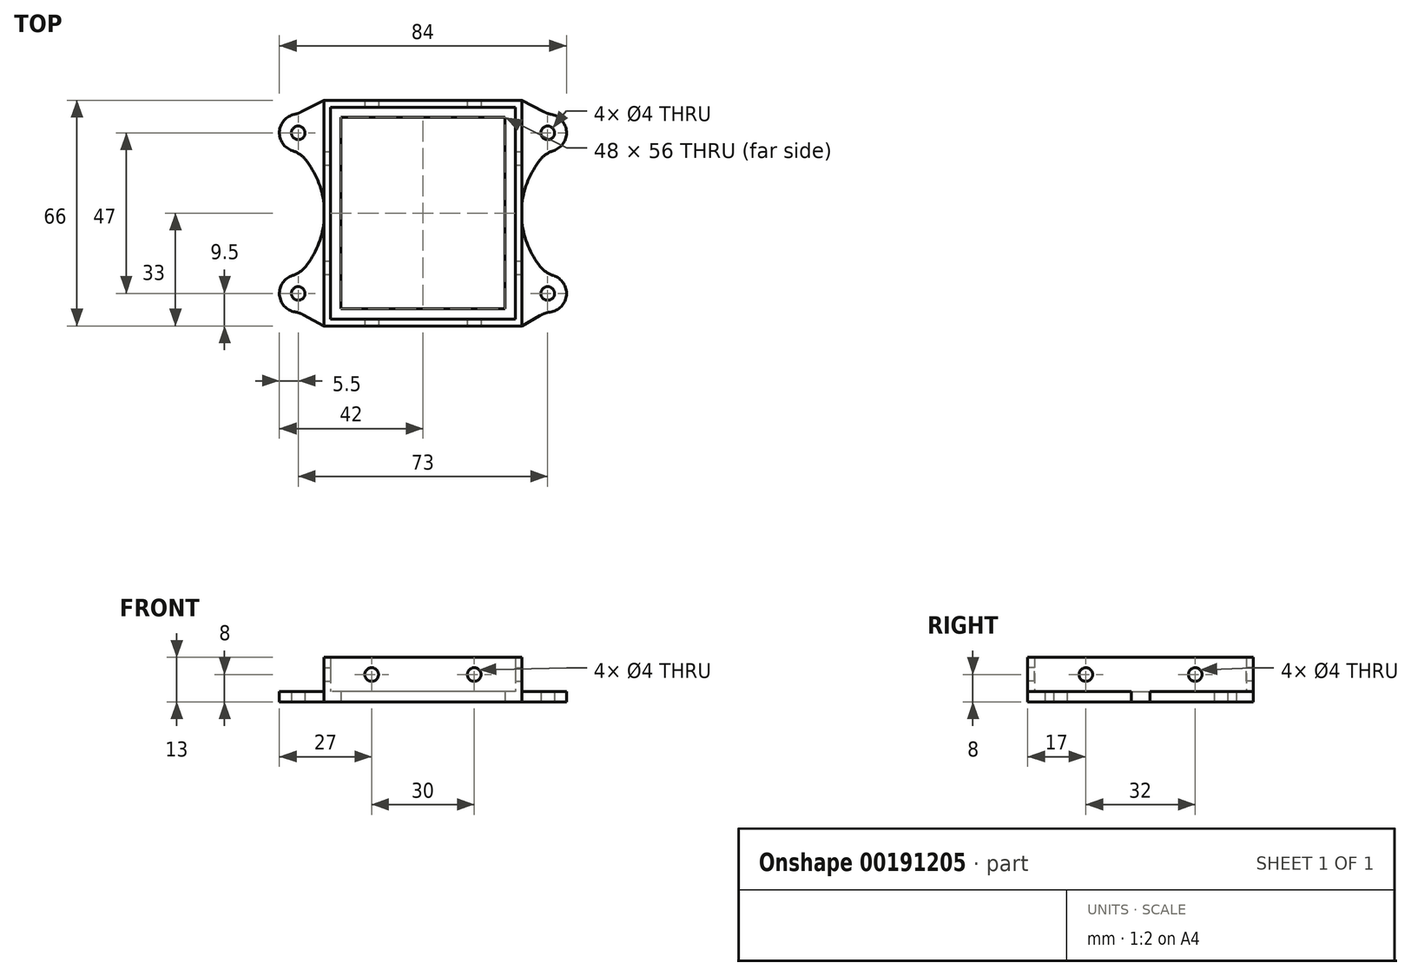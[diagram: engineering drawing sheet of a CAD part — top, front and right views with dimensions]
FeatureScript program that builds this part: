
annotation { "Feature Type Name" : "Feature", "Feature Type Description" : "" }
export const myFeature = defineFeature(function(context is Context, id is Id, definition is map)
    precondition{}
    {
        {
            var Q0;
            Q0=qCreatedBy(makeId("Top.planeOp"),FACE);
            var sketch = newSketch(context, id + "F0", { "sketchPlane" : qUnion([Q0])});
            skLineSegment(sketch, "E0.bottom", {"start": v(29, -33) * mm, "end": v(-29, -33) * mm});
            skLineSegment(sketch, "E0.top", {"start": v(29, 33) * mm, "end": v(-29, 33) * mm});
            skLineSegment(sketch, "E0.left", {"start": v(29, -2.74) * mm, "end": v(29, 2.74) * mm});
            skLineSegment(sketch, "E0.right", {"start": v(-29, -2.74) * mm, "end": v(-29, 2.74) * mm});
            skPoint(sketch, "E0.middle", {"position": v(0, 0) * mm});
            skCircle(sketch, "E1", {"center": v(-36.5, 23.5) * mm, "radius": 2 * mm});
            skCircle(sketch, "E2", {"center": v(-36.5, -23.5) * mm, "radius": 2 * mm});
            skCircle(sketch, "E3", {"center": v(36.5, -23.5) * mm, "radius": 2 * mm});
            skCircle(sketch, "E4", {"center": v(36.5, 23.5) * mm, "radius": 2 * mm});
            skArc(sketch, "E5", {"start": v(38.16, 18.26) * mm, "mid": v(41.99, 23.84) * mm, "end": v(37.51, 28.9) * mm});
            skArc(sketch, "E6", {"start": v(37.2, -28.96) * mm, "mid": v(41.98, -24) * mm, "end": v(38.16, -18.26) * mm});
            skArc(sketch, "E7", {"start": v(-38.16, -18.26) * mm, "mid": v(-41.99, -23.87) * mm, "end": v(-37.44, -28.92) * mm});
            skArc(sketch, "E8", {"start": v(-37.6, 28.89) * mm, "mid": v(-42, 23.8) * mm, "end": v(-38.16, 18.26) * mm});
            skArc(sketch, "E9", {"start": v(-34.34, -15.64) * mm, "mid": v(-28.85, 0) * mm, "end": v(-34.34, 15.64) * mm});
            skArc(sketch, "E10", {"start": v(34.34, 15.64) * mm, "mid": v(28.85, 0) * mm, "end": v(34.34, -15.64) * mm});
            skLineSegment(sketch, "E11", {"start": v(-29, 33) * mm, "end": v(-35.52, 29.62) * mm});
            skLineSegment(sketch, "E12", {"start": v(29, 33) * mm, "end": v(35.24, 29.7) * mm});
            skLineSegment(sketch, "E13", {"start": v(-35, -29.76) * mm, "end": v(-29, -33) * mm});
            skLineSegment(sketch, "E14", {"start": v(34.19, -29.98) * mm, "end": v(29, -33) * mm});
            skPoint(sketch, "E15.visualSharp", {"position": v(35.92, -28.97) * mm});
            skArc(sketch, "E15.filletArc", {"start": v(37.2, -28.96) * mm, "mid": v(35.64, -29.32) * mm, "end": v(34.19, -29.98) * mm});
            skPoint(sketch, "E16.visualSharp", {"position": v(-36.41, -29) * mm});
            skArc(sketch, "E16.filletArc", {"start": v(-35, -29.76) * mm, "mid": v(-36.18, -29.24) * mm, "end": v(-37.44, -28.92) * mm});
            skPoint(sketch, "E17.visualSharp", {"position": v(-36.74, 29) * mm});
            skArc(sketch, "E17.filletArc", {"start": v(-37.6, 28.89) * mm, "mid": v(-36.54, 29.18) * mm, "end": v(-35.52, 29.62) * mm});
            skPoint(sketch, "E18.visualSharp", {"position": v(36.56, 29) * mm});
            skArc(sketch, "E18.filletArc", {"start": v(35.24, 29.7) * mm, "mid": v(36.35, 29.22) * mm, "end": v(37.51, 28.9) * mm});
            skPoint(sketch, "E19.visualSharp", {"position": v(36.5, 18) * mm});
            skArc(sketch, "E19.filletArc", {"start": v(38.16, 18.26) * mm, "mid": v(36.06, 17.23) * mm, "end": v(34.34, 15.64) * mm});
            skPoint(sketch, "E20.visualSharp", {"position": v(36.5, -18) * mm});
            skArc(sketch, "E20.filletArc", {"start": v(34.34, -15.64) * mm, "mid": v(36.06, -17.23) * mm, "end": v(38.16, -18.26) * mm});
            skPoint(sketch, "E21.visualSharp", {"position": v(-36.5, -18) * mm});
            skArc(sketch, "E21.filletArc", {"start": v(-38.16, -18.26) * mm, "mid": v(-36.06, -17.23) * mm, "end": v(-34.34, -15.64) * mm});
            skPoint(sketch, "E22.visualSharp", {"position": v(-36.5, 18) * mm});
            skArc(sketch, "E22.filletArc", {"start": v(-34.34, 15.64) * mm, "mid": v(-36.06, 17.23) * mm, "end": v(-38.16, 18.26) * mm});
            skLineSegment(sketch, "E23.bottom", {"start": v(24, -28) * mm, "end": v(-24, -28) * mm});
            skLineSegment(sketch, "E23.top", {"start": v(24, 28) * mm, "end": v(-24, 28) * mm});
            skLineSegment(sketch, "E23.left", {"start": v(24, -28) * mm, "end": v(24, 28) * mm});
            skLineSegment(sketch, "E23.right", {"start": v(-24, -28) * mm, "end": v(-24, 28) * mm});
            skSolve(sketch);
        }
        {
            var Q0;
            Q0 = qSketchRegion(id + "F0", true);
            extrude(context, id + "F1", {"entities" : qUnion([Q0]), "depth" : 3 * mm});
        }
        {
            var Q0;
            Q0=makeQuery(id+"F1.opExtrude","CAP_FACE",FACE,{"disambiguationData":[OSD([sQuery(id+"F0.wireOp",EDGE,"E0.bottom"),sQuery(id+"F0.wireOp",EDGE,"E0.top"),sQuery(id+"F0.wireOp",EDGE,"E0.left"),sQuery(id+"F0.wireOp",EDGE,"E0.right"),sQuery(id+"F0.wireOp",EDGE,"E1"),sQuery(id+"F0.wireOp",EDGE,"E2"),sQuery(id+"F0.wireOp",EDGE,"E3"),sQuery(id+"F0.wireOp",EDGE,"E4"),sQuery(id+"F0.wireOp",EDGE,"E5"),sQuery(id+"F0.wireOp",EDGE,"E6"),sQuery(id+"F0.wireOp",EDGE,"E7"),sQuery(id+"F0.wireOp",EDGE,"E8"),sQuery(id+"F0.wireOp",EDGE,"E9"),sQuery(id+"F0.wireOp",EDGE,"E10"),sQuery(id+"F0.wireOp",EDGE,"E11"),sQuery(id+"F0.wireOp",EDGE,"E12"),sQuery(id+"F0.wireOp",EDGE,"E13"),sQuery(id+"F0.wireOp",EDGE,"E14"),sQuery(id+"F0.wireOp",EDGE,"E15.filletArc"),sQuery(id+"F0.wireOp",EDGE,"E16.filletArc"),sQuery(id+"F0.wireOp",EDGE,"E17.filletArc"),sQuery(id+"F0.wireOp",EDGE,"E18.filletArc"),sQuery(id+"F0.wireOp",EDGE,"E19.filletArc"),sQuery(id+"F0.wireOp",EDGE,"E20.filletArc"),sQuery(id+"F0.wireOp",EDGE,"E21.filletArc"),sQuery(id+"F0.wireOp",EDGE,"E22.filletArc")])],"isStart":false});
            var sketch = newSketch(context, id + "F2", { "sketchPlane" : qUnion([Q0])});
            skLineSegment(sketch, "E24.bottom", {"start": v(29, -33) * mm, "end": v(-29, -33) * mm});
            skLineSegment(sketch, "E24.top", {"start": v(29, 33) * mm, "end": v(-29, 33) * mm});
            skLineSegment(sketch, "E24.left", {"start": v(29, -33) * mm, "end": v(29, 33) * mm});
            skLineSegment(sketch, "E24.right", {"start": v(-29, -33) * mm, "end": v(-29, 33) * mm});
            skPoint(sketch, "E24.middle", {"position": v(0, 0) * mm});
            skLineSegment(sketch, "E25.bottom", {"start": v(27, -31) * mm, "end": v(-27, -31) * mm});
            skLineSegment(sketch, "E25.top", {"start": v(27, 31) * mm, "end": v(-27, 31) * mm});
            skLineSegment(sketch, "E25.left", {"start": v(27, -31) * mm, "end": v(27, 31) * mm});
            skLineSegment(sketch, "E25.right", {"start": v(-27, -31) * mm, "end": v(-27, 31) * mm});
            skSolve(sketch);
        }
        {
            var Q0;
            Q0 = qSketchRegion(id + "F2", true);
            extrude(context, id + "F3", {"entities" : qUnion([Q0]), "operationType" : NewBodyOperationType.ADD, "depth" : 10 * mm});
        }
        {
            var Q0;
            Q0=makeQuery(id+"F3.boolean.opBoolean","MERGE",FACE,{"derivedFrom":[makeQuery(id+"F1.opExtrude","SWEPT_FACE",FACE,{"disambiguationData":[OSD([sQuery(id+"F0.wireOp",EDGE,"E0.bottom")])]}),makeQuery(id+"F3.opExtrude","SWEPT_FACE",FACE,{"disambiguationData":[OSD([sQuery(id+"F2.wireOp",EDGE,"E24.bottom")])]})]});
            var sketch = newSketch(context, id + "F4", { "sketchPlane" : qUnion([Q0])});
            skCircle(sketch, "E26", {"center": v(-15, 8) * mm, "radius": 2 * mm});
            skPoint(sketch, "E26.centerSnap0", {"position": v(-29, 8) * mm});
            skCircle(sketch, "E27", {"center": v(15, 8) * mm, "radius": 2 * mm});
            skPoint(sketch, "E27.centerSnap0", {"position": v(29, 8) * mm});
            skSolve(sketch);
        }
        {
            var Q0;
            Q0 = qSketchRegion(id + "F4", true);
            extrude(context, id + "F5", {"entities" : qUnion([Q0]), "operationType" : NewBodyOperationType.REMOVE, "oppositeDirection" : true, "depth" : 150 * mm});
        }
        {
            var Q0;
            Q0=makeQuery(id+"F3.boolean.opBoolean","MERGE",FACE,{"derivedFrom":[makeQuery(id+"F1.opExtrude","SWEPT_FACE",FACE,{"disambiguationData":[OSD([sQuery(id+"F0.wireOp",EDGE,"E0.left")])]}),makeQuery(id+"F3.opExtrude","SWEPT_FACE",FACE,{"disambiguationData":[OSD([sQuery(id+"F2.wireOp",EDGE,"E24.left")])]})]});
            var sketch = newSketch(context, id + "F6", { "sketchPlane" : qUnion([Q0])});
            skCircle(sketch, "E28", {"center": v(-16, 8) * mm, "radius": 2 * mm});
            skPoint(sketch, "E28.centerSnap0", {"position": v(-33, 8) * mm});
            skCircle(sketch, "E29", {"center": v(16, 8) * mm, "radius": 2 * mm});
            skPoint(sketch, "E29.centerSnap0", {"position": v(33, 8) * mm});
            skSolve(sketch);
        }
        {
            var Q0;
            Q0 = qSketchRegion(id + "F6", true);
            extrude(context, id + "F7", {"entities" : qUnion([Q0]), "operationType" : NewBodyOperationType.REMOVE, "oppositeDirection" : true, "depth" : 150 * mm});
        }
    });
